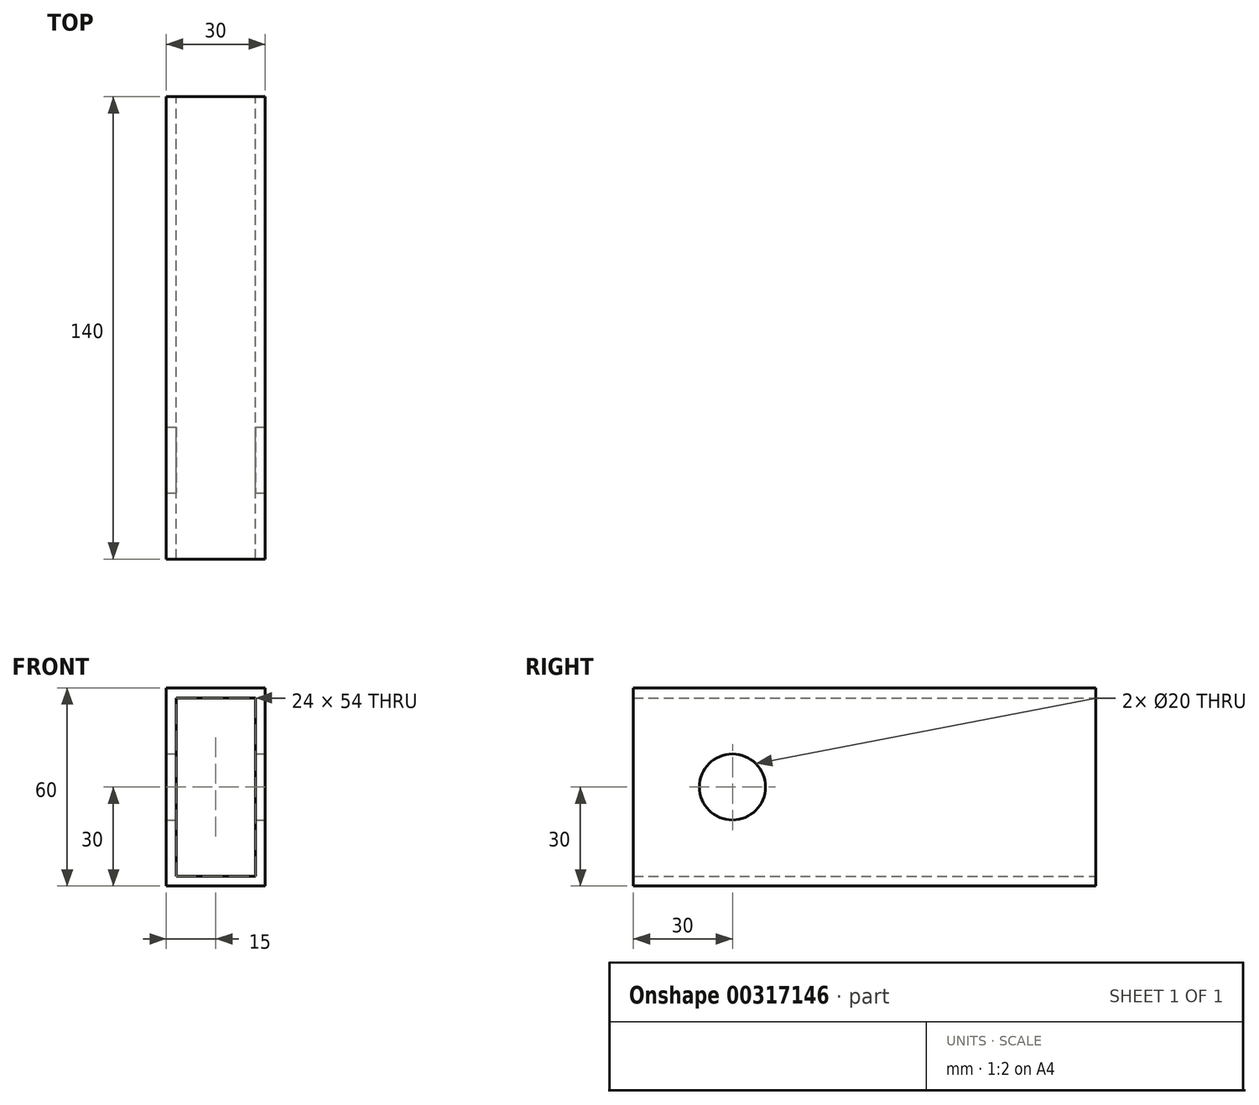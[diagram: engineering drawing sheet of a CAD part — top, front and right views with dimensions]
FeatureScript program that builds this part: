
annotation { "Feature Type Name" : "Feature", "Feature Type Description" : "" }
export const myFeature = defineFeature(function(context is Context, id is Id, definition is map)
    precondition{}
    {
        {
            var Q0;
            Q0=qCreatedBy(makeId("Front.planeOp"),FACE);
            var sketch = newSketch(context, id + "F0", { "sketchPlane" : qUnion([Q0])});
            skLineSegment(sketch, "E0.bottom", {"start": v(15, 30) * mm, "end": v(-15, 30) * mm});
            skLineSegment(sketch, "E0.top", {"start": v(15, -30) * mm, "end": v(-15, -30) * mm});
            skLineSegment(sketch, "E0.left", {"start": v(15, 30) * mm, "end": v(15, -30) * mm});
            skLineSegment(sketch, "E0.right", {"start": v(-15, 30) * mm, "end": v(-15, -30) * mm});
            skPoint(sketch, "E0.middle", {"position": v(0, 0) * mm});
            skLineSegment(sketch, "E1.0", {"start": v(12, -27) * mm, "end": v(-12, -27) * mm});
            skLineSegment(sketch, "E1.1", {"start": v(12, 27) * mm, "end": v(12, -27) * mm});
            skLineSegment(sketch, "E1.2", {"start": v(12, 27) * mm, "end": v(-12, 27) * mm});
            skLineSegment(sketch, "E1.3", {"start": v(-12, 27) * mm, "end": v(-12, -27) * mm});
            skSolve(sketch);
        }
        {
            var Q0;
            Q0=makeQuery(id+"F0.imprint","IMPRINT",FACE,{"disambiguationData":[TD([[makeQuery(id+"F0.imprint","IMPRINT",EDGE,{"derivedFrom":sQuery(id+"F0.wireOp",EDGE,"E0.bottom")}),1.0]])]});
            extrude(context, id + "F1", {"entities" : qUnion([Q0]), "endBound" : BoundingType.SYMMETRIC, "depth" : (60 + 10 + 60 + 10) * mm});
        }
        {
            var Q0;
            Q0=makeQuery(id+"F1.opExtrude","SWEPT_FACE",FACE,{"disambiguationData":[OSD([sQuery(id+"F0.wireOp",EDGE,"E0.left")])]});
            var sketch = newSketch(context, id + "F2", { "sketchPlane" : qUnion([Q0])});
            skPoint(sketch, "E2", {"position": v(-40, 0) * mm});
            skPoint(sketch, "E3", {"position": v(327.29, -21.45) * mm});
            skSolve(sketch);
        }
        {
            var Q0;
            Q0=sQuery(id+"F2.wireOp",VERTEX,"E2");
            var Q1;
            Q1=makeQuery(id+"F1.opExtrude","SWEPT_BODY",BODY,{"disambiguationData":[OSD([sQuery(id+"F0.wireOp",EDGE,"E0.bottom"),sQuery(id+"F0.wireOp",EDGE,"E0.top"),sQuery(id+"F0.wireOp",EDGE,"E0.left"),sQuery(id+"F0.wireOp",EDGE,"E0.right"),sQuery(id+"F0.wireOp",EDGE,"E1.0"),sQuery(id+"F0.wireOp",EDGE,"E1.1"),sQuery(id+"F0.wireOp",EDGE,"E1.2"),sQuery(id+"F0.wireOp",EDGE,"E1.3")])]});
            hole(context, id + "F3", {"style" : HoleStyle.SIMPLE, "endStyle" : HoleEndStyle.THROUGH, "holeDiameter" : 20 * mm, "tappedDepth" : 12 * mm, "tapClearance" : 3, "locations" : qUnion([Q0]), "scope" : qUnion([Q1])});
        }
    });
